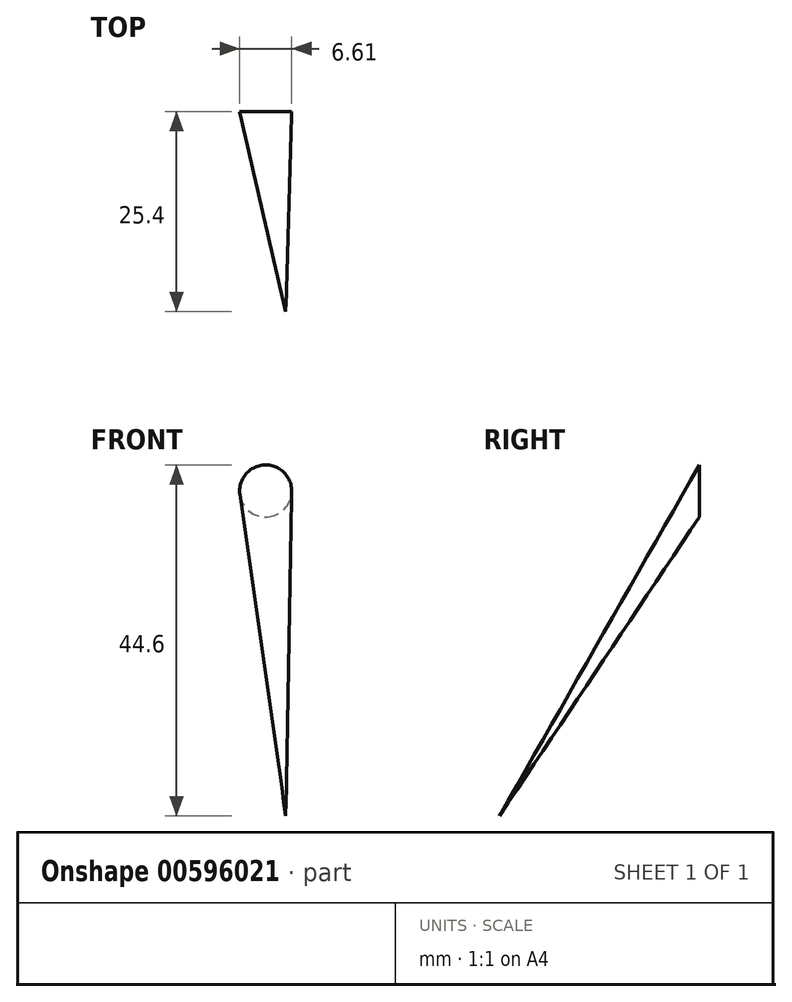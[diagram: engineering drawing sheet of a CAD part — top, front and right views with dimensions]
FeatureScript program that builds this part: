
annotation { "Feature Type Name" : "Feature", "Feature Type Description" : "" }
export const myFeature = defineFeature(function(context is Context, id is Id, definition is map)
    precondition{}
    {
        {
            var Q0;
            Q0=qCreatedBy(makeId("Front.planeOp"),FACE);
            var sketch = newSketch(context, id + "F0", { "sketchPlane" : qUnion([Q0])});
            skCircle(sketch, "E0", {"center": v(-52.83, 62.03) * mm, "radius": 3.3 * mm});
            skSolve(sketch);
        }
        {
            var Q0;
            Q0=qCreatedBy(makeId("Front.planeOp"),FACE);
            cPlane(context, id + "F1", {"entities" : qUnion([Q0]), "cplaneType" : CPlaneType.OFFSET, "offset" : 25.4 * mm, "width" : 152.4 * mm, "height" : 152.4 * mm});
        }
        {
            var Q0;
            Q0=qCreatedBy(id+"F1.planeOp",FACE);
            var sketch = newSketch(context, id + "F2", { "sketchPlane" : qUnion([Q0])});
            skCircle(sketch, "E1", {"center": v(-50.27, 20.73) * mm, "radius": 1.98 * mm});
            skSolve(sketch);
        }
        {
            var Q0;
            Q0=makeQuery(id+"F0.imprint","IMPRINT",FACE,{"disambiguationData":[TD([[makeQuery(id+"F0.imprint","IMPRINT",EDGE,{"derivedFrom":sQuery(id+"F0.wireOp",EDGE,"E0")}),1.0]])]});
            var Q1;
            Q1=sQuery(id+"F2.wireOp",VERTEX,"E1.center");
            loft(context, id + "F3", {"sheetProfilesArray" : [{ "sheetProfileEntities" : qUnion([Q0]) }, { "sheetProfileEntities" : qUnion([Q1]) }]});
        }
    });
